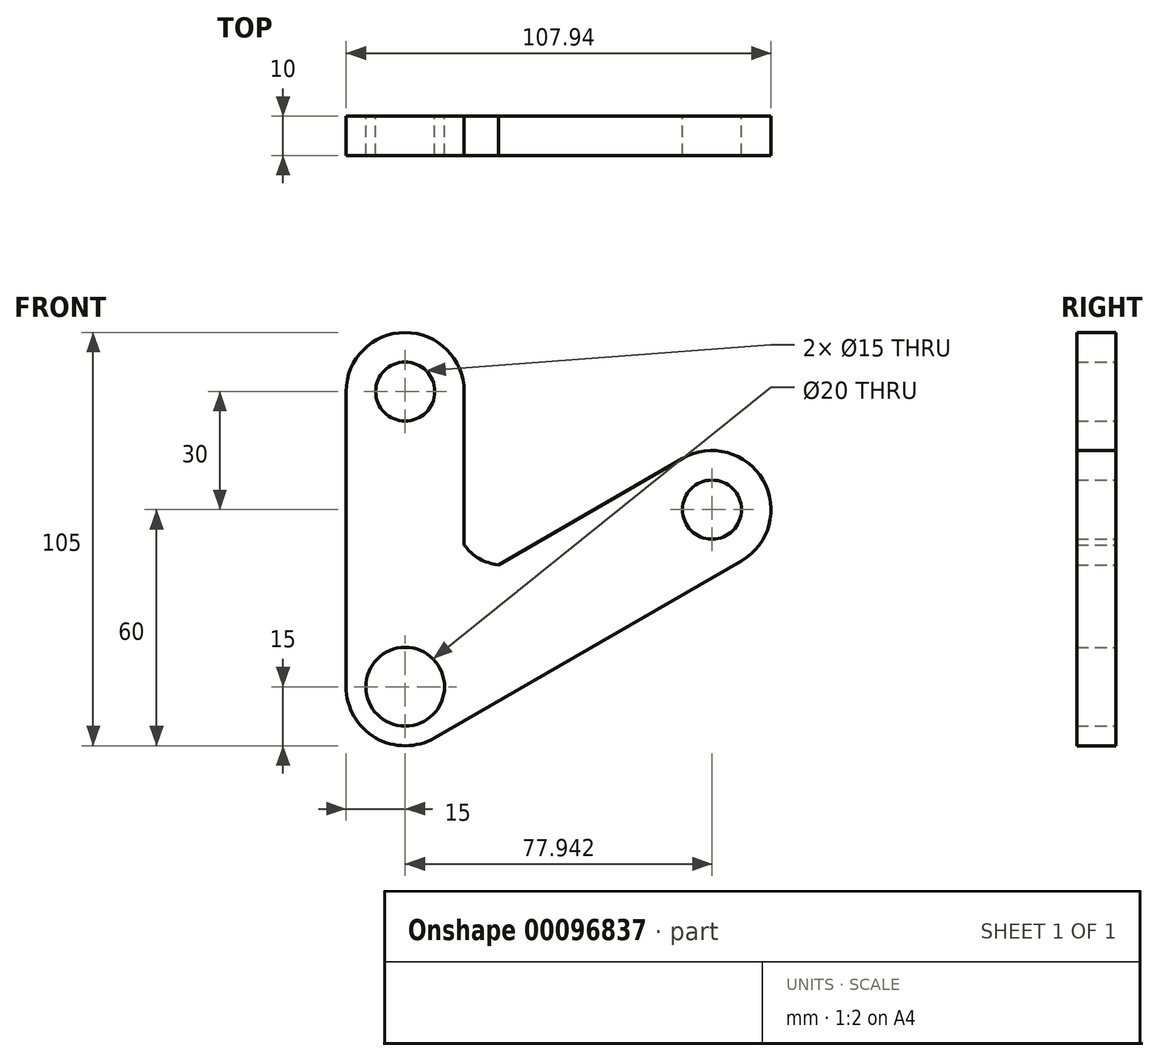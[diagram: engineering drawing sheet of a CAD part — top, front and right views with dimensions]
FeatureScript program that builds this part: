
annotation { "Feature Type Name" : "Feature", "Feature Type Description" : "" }
export const myFeature = defineFeature(function(context is Context, id is Id, definition is map)
    precondition{}
    {
        {
            var Q0;
            Q0=qCreatedBy(makeId("Front.planeOp"),FACE);
            var sketch = newSketch(context, id + "F0", { "sketchPlane" : qUnion([Q0])});
            skCircle(sketch, "E0", {"center": v(0, 0) * mm, "radius": 10 * mm});
            skLineSegment(sketch, "E1", {"start": v(0, 0) * mm, "end": v(0, 75) * mm, "construction": true});
            skCircle(sketch, "E2", {"center": v(0, 75) * mm, "radius": 7.5 * mm});
            skCircle(sketch, "E3", {"center": v(0, 75) * mm, "radius": 15 * mm});
            skCircle(sketch, "E4", {"center": v(0, 0) * mm, "radius": 15 * mm});
            skLineSegment(sketch, "E5", {"start": v(0, 75) * mm, "end": v(-36.22, 75) * mm, "construction": true});
            skLineSegment(sketch, "E6", {"start": v(-15, 75) * mm, "end": v(-15, 0) * mm});
            skLineSegment(sketch, "E7", {"start": v(0, 75) * mm, "end": v(31.85, 75) * mm, "construction": true});
            skLineSegment(sketch, "E8", {"start": v(0, 0) * mm, "end": v(77.94, 45) * mm, "construction": true});
            skCircle(sketch, "E9", {"center": v(77.94, 45) * mm, "radius": 7.5 * mm});
            skCircle(sketch, "E10", {"center": v(77.94, 45) * mm, "radius": 15 * mm});
            skLineSegment(sketch, "E11", {"start": v(0, 0) * mm, "end": v(16.42, -28.43) * mm, "construction": true});
            skLineSegment(sketch, "E12", {"start": v(77.94, 45) * mm, "end": v(95.55, 14.5) * mm, "construction": true});
            skLineSegment(sketch, "E13", {"start": v(7.5, -13) * mm, "end": v(85.44, 32) * mm});
            skLineSegment(sketch, "E14", {"start": v(77.94, 45) * mm, "end": v(-28.8, 45) * mm, "construction": true});
            skLineSegment(sketch, "E15", {"start": v(77.94, 45) * mm, "end": v(62.14, 72.37) * mm, "construction": true});
            skLineSegment(sketch, "E16", {"start": v(15, 75) * mm, "end": v(15, 0) * mm, "construction": true});
            skLineSegment(sketch, "E17", {"start": v(0, 0) * mm, "end": v(-21.1, 36.54) * mm, "construction": true});
            skLineSegment(sketch, "E18", {"start": v(70.44, 58) * mm, "end": v(-7.5, 13) * mm, "construction": true});
            skLineSegment(sketch, "E19", {"start": v(0, 0) * mm, "end": v(47.92, 83) * mm, "construction": true});
            skLineSegment(sketch, "E20", {"start": v(15, 25.98) * mm, "end": v(15, 35.98) * mm, "construction": true});
            skLineSegment(sketch, "E21", {"start": v(15, 25.98) * mm, "end": v(23.66, 30.98) * mm, "construction": true});
            skArc(sketch, "E22", {"start": v(15, 35.98) * mm, "mid": v(18.8, 32.57) * mm, "end": v(23.66, 30.98) * mm});
            skPoint(sketch, "E22.third.point", {"position": v(36.18, 48.66) * mm});
            skLineSegment(sketch, "E23", {"start": v(15, 75) * mm, "end": v(15, 35.98) * mm});
            skLineSegment(sketch, "E24", {"start": v(70.44, 58) * mm, "end": v(23.66, 30.98) * mm});
            skSolve(sketch);
        }
        {
            var Q0;
            Q0 = qSketchRegion(id + "F0", true);
            extrude(context, id + "F1", {"entities" : qUnion([Q0]), "depth" : 10 * mm});
        }
    });
